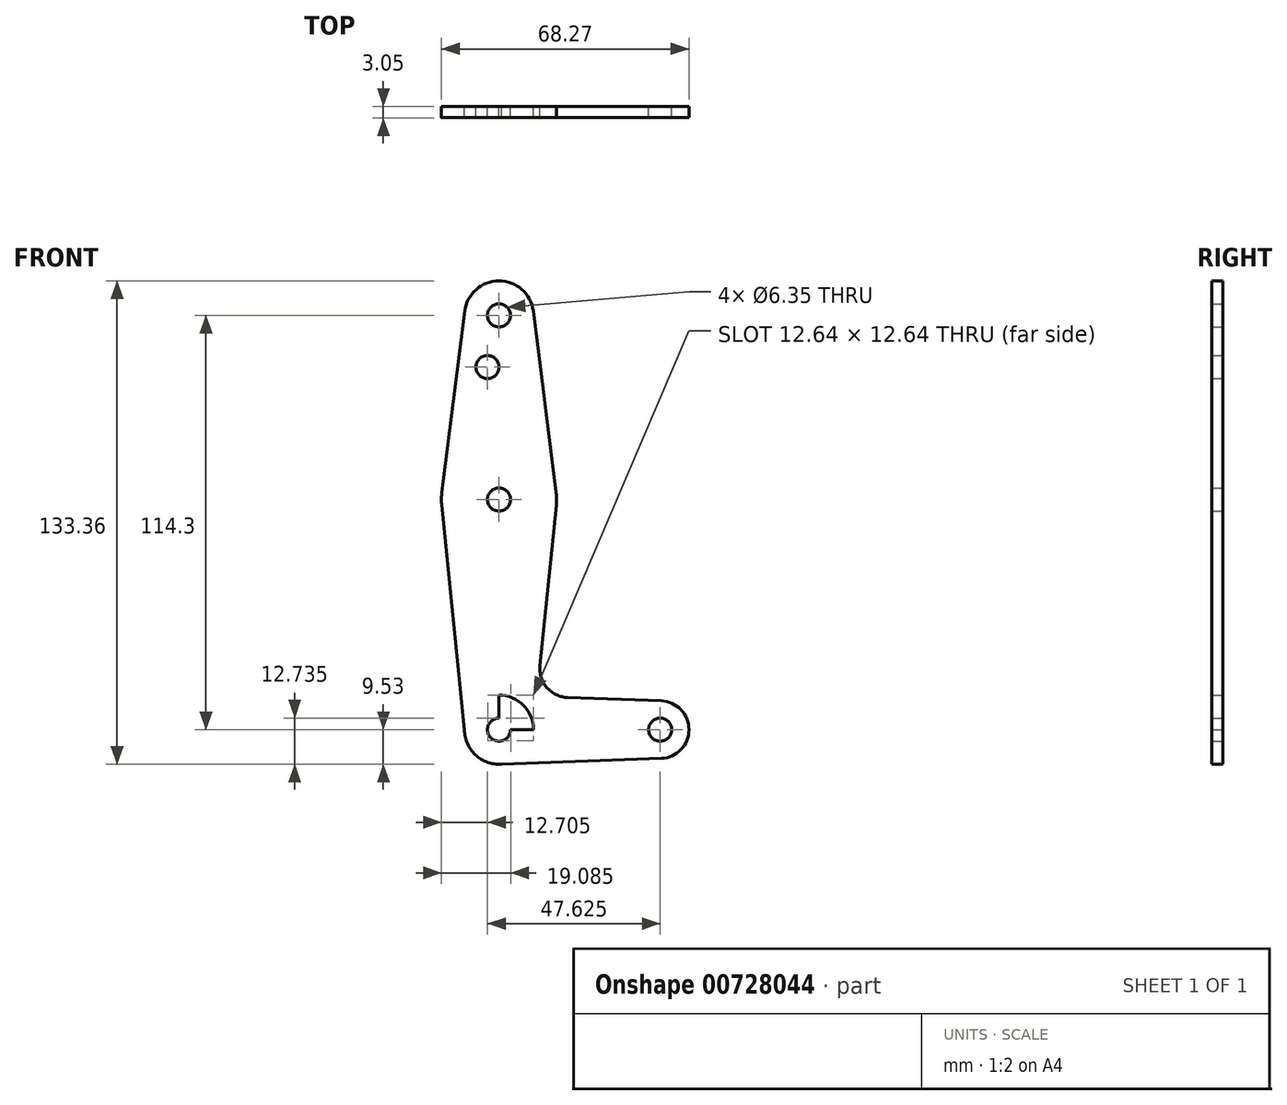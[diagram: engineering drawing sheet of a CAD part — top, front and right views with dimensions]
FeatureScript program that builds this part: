
annotation { "Feature Type Name" : "Feature", "Feature Type Description" : "" }
export const myFeature = defineFeature(function(context is Context, id is Id, definition is map)
    precondition{}
    {
        {
            var Q0;
            Q0=qCreatedBy(makeId("Front.planeOp"),FACE);
            var sketch = newSketch(context, id + "F0", { "sketchPlane" : qUnion([Q0])});
            skLineSegment(sketch, "E0", {"start": v(0, 0) * mm, "end": v(0, 57.15) * mm});
            skLineSegment(sketch, "E1", {"start": v(0, 114.3) * mm, "end": v(0, 57.15) * mm});
            skLineSegment(sketch, "E2", {"start": v(0, 0) * mm, "end": v(44.45, 0) * mm});
            skLineSegment(sketch, "E3", {"start": v(44.45, 0) * mm, "end": v(0, 0) * mm});
            skCircle(sketch, "E4", {"center": v(0, 0) * mm, "radius": 9.53 * mm});
            skCircle(sketch, "E5", {"center": v(44.45, 0) * mm, "radius": 7.94 * mm});
            skCircle(sketch, "E6", {"center": v(0, 114.3) * mm, "radius": 9.53 * mm});
            skLineSegment(sketch, "E7", {"start": v(0, 114.3) * mm, "end": v(0, 0) * mm});
            skCircle(sketch, "E8", {"center": v(0, 63.5) * mm, "radius": 15.88 * mm});
            skLineSegment(sketch, "E9", {"start": v(0, -9.53) * mm, "end": v(44.73, -7.93) * mm});
            skLineSegment(sketch, "E10", {"start": v(0, 9.53) * mm, "end": v(44.73, 7.93) * mm});
            skLineSegment(sketch, "E11", {"start": v(44.73, 7.93) * mm, "end": v(18.93, 8.85) * mm});
            skLineSegment(sketch, "E12", {"start": v(-9.45, 115.5) * mm, "end": v(-15.75, 65.48) * mm});
            skLineSegment(sketch, "E13", {"start": v(9.45, 115.5) * mm, "end": v(15.75, 65.48) * mm});
            skCircle(sketch, "E14", {"center": v(0, 63.5) * mm, "radius": 3.18 * mm});
            skCircle(sketch, "E15", {"center": v(0, 0) * mm, "radius": 3.18 * mm});
            skCircle(sketch, "E16", {"center": v(44.45, 0) * mm, "radius": 3.18 * mm});
            skCircle(sketch, "E17", {"center": v(0, 114.3) * mm, "radius": 3.18 * mm});
            skLineSegment(sketch, "E18", {"start": v(0, 100.03) * mm, "end": v(0, 63.5) * mm});
            skCircle(sketch, "E19", {"center": v(-3.18, 100.03) * mm, "radius": 3.18 * mm});
            skLineSegment(sketch, "E20", {"start": v(-9.53, 0) * mm, "end": v(-15.8, 61.9) * mm});
            skLineSegment(sketch, "E21", {"start": v(11.3, 17.6) * mm, "end": v(15.8, 61.9) * mm});
            skArc(sketch, "E22.filletArc", {"start": v(11.3, 17.6) * mm, "mid": v(13.22, 11.57) * mm, "end": v(18.93, 8.85) * mm});
            skSolve(sketch);
        }
        {
            var Q0;
            Q0 = qSketchRegion(id + "F0", true);
            var Q1;
            {var subQ2=sQuery(id+"F0.wireOp",EDGE,"E4");var subQ7=sQuery(id+"F0.wireOp",EDGE,"E3");var subQ8=makeQuery(id+"F0.imprint","INTERSECT",VERTEX,{"derivedFrom":[subQ7,subQ2]});Q1=makeQuery(id+"F0.imprint","IMPRINT",FACE,{"disambiguationData":[TD([[makeQuery(id+"F0.imprint","IMPRINT",EDGE,{"disambiguationData":[TD([[subQ8,-1.0]])],"derivedFrom":subQ7}),-1.0]])]});}
            extrude(context, id + "F1", {"entities" : qUnion([Q0, Q1]), "depth" : 3.05 * mm, "offsetDistance" : 25.4 * mm});
        }
    });
